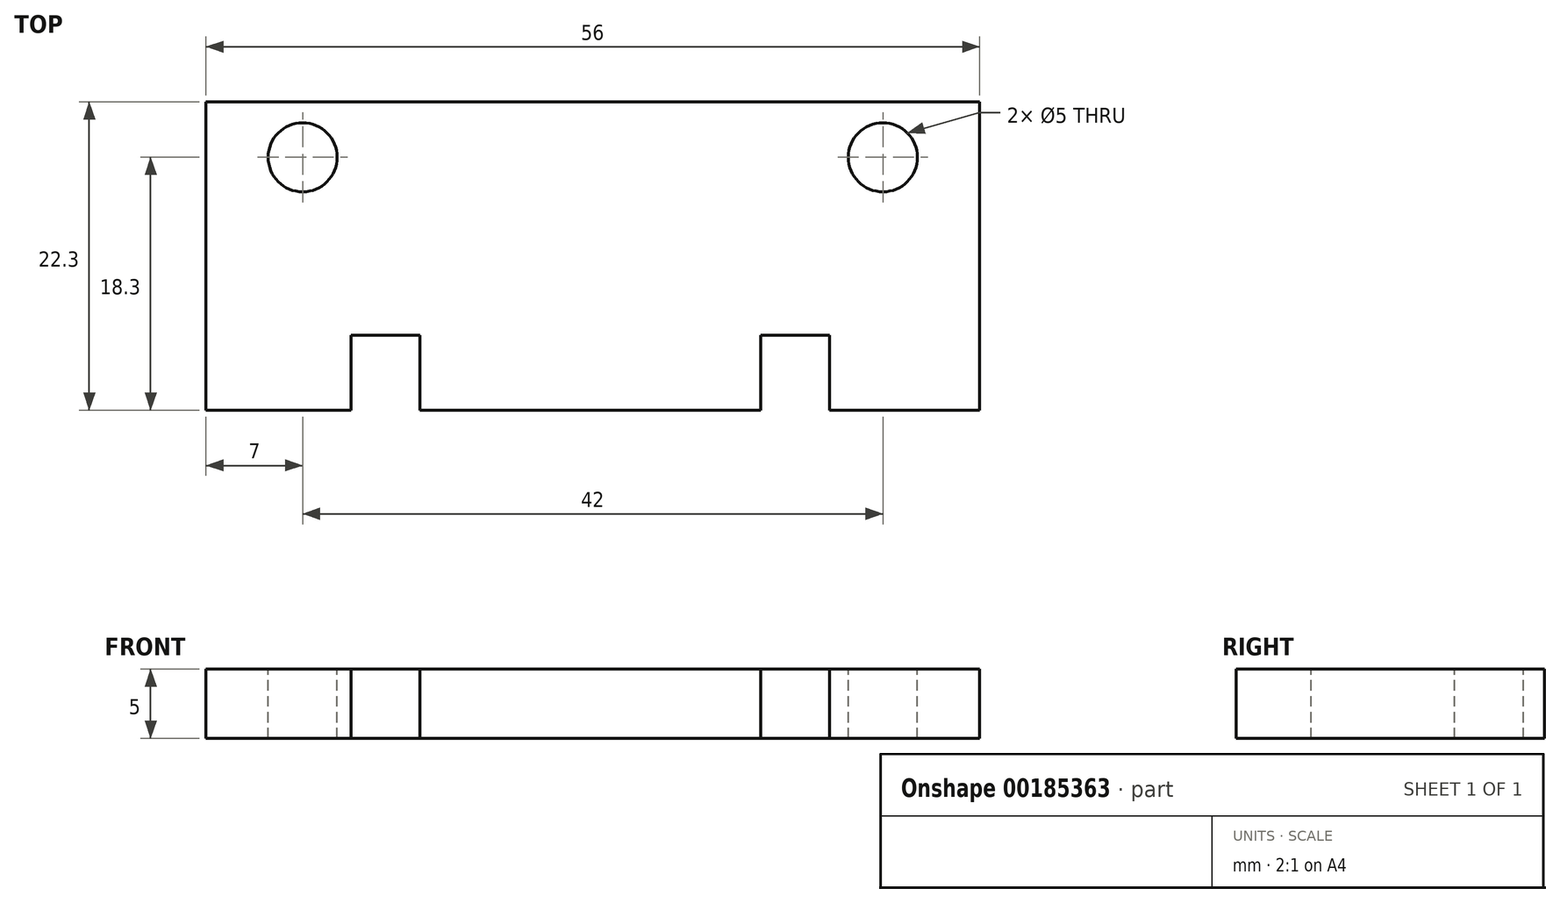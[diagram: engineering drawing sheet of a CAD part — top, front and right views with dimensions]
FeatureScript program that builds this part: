
annotation { "Feature Type Name" : "Feature", "Feature Type Description" : "" }
export const myFeature = defineFeature(function(context is Context, id is Id, definition is map)
    precondition{}
    {
        {
            var Q0;
            Q0=qCreatedBy(makeId("Top.planeOp"),FACE);
            var sketch = newSketch(context, id + "F0", { "sketchPlane" : qUnion([Q0])});
            skLineSegment(sketch, "E0.bottom", {"start": v(28, -8.65) * mm, "end": v(-28, -8.65) * mm, "construction": true});
            skLineSegment(sketch, "E0.top", {"start": v(28, 8.65) * mm, "end": v(-28, 8.65) * mm});
            skLineSegment(sketch, "E0.left", {"start": v(28, -8.65) * mm, "end": v(28, 8.65) * mm});
            skLineSegment(sketch, "E0.right", {"start": v(-28, -8.65) * mm, "end": v(-28, 8.65) * mm});
            skPoint(sketch, "E0.middle", {"position": v(0, 0) * mm});
            skLineSegment(sketch, "E1", {"start": v(-28, -8.65) * mm, "end": v(-28, -13.65) * mm});
            skLineSegment(sketch, "E2", {"start": v(-28, -13.65) * mm, "end": v(28, -13.65) * mm});
            skLineSegment(sketch, "E3", {"start": v(28, -13.65) * mm, "end": v(28, -8.65) * mm});
            skSolve(sketch);
        }
        {
            var Q0;
            Q0=makeQuery(id+"F0.imprint","IMPRINT",FACE,{"disambiguationData":[TD([[makeQuery(id+"F0.imprint","IMPRINT",EDGE,{"derivedFrom":sQuery(id+"F0.wireOp",EDGE,"E0.top")}),1.0]])]});
            extrude(context, id + "F1", {"entities" : qUnion([Q0]), "depth" : 5 * mm});
        }
        {
            var Q0;
            Q0=makeQuery(id+"F1.opExtrude","CAP_FACE",FACE,{"disambiguationData":[OSD([sQuery(id+"F0.wireOp",EDGE,"E0.bottom"),sQuery(id+"F0.wireOp",EDGE,"E0.top"),sQuery(id+"F0.wireOp",EDGE,"E0.left"),sQuery(id+"F0.wireOp",EDGE,"E0.right")])],"isStart":false});
            var sketch = newSketch(context, id + "F2", { "sketchPlane" : qUnion([Q0])});
            skCircle(sketch, "E4", {"center": v(-21, 4.65) * mm, "radius": 2.5 * mm});
            skCircle(sketch, "E5", {"center": v(21, 4.65) * mm, "radius": 2.5 * mm});
            skLineSegment(sketch, "E6", {"start": v(-28, 4.65) * mm, "end": v(28, 4.65) * mm, "construction": true});
            skLineSegment(sketch, "E7", {"start": v(-21, 4.65) * mm, "end": v(0, 0) * mm});
            skLineSegment(sketch, "E8", {"start": v(0, 0) * mm, "end": v(21, 4.65) * mm});
            skSolve(sketch);
        }
        {
            var Q0;
            Q0 = qSketchRegion(id + "F2", true);
            extrude(context, id + "F3", {"entities" : qUnion([Q0]), "operationType" : NewBodyOperationType.REMOVE, "oppositeDirection" : true, "depth" : 5 * mm});
        }
        {
            var Q0;
            Q0=makeQuery(id+"F1.opExtrude","CAP_FACE",FACE,{"disambiguationData":[OSD([sQuery(id+"F0.wireOp",EDGE,"E0.top"),sQuery(id+"F0.wireOp",EDGE,"E0.left"),sQuery(id+"F0.wireOp",EDGE,"E0.right"),sQuery(id+"F0.wireOp",EDGE,"E1"),sQuery(id+"F0.wireOp",EDGE,"E2"),sQuery(id+"F0.wireOp",EDGE,"E3")])],"isStart":false});
            var sketch = newSketch(context, id + "F4", { "sketchPlane" : qUnion([Q0])});
            skLineSegment(sketch, "E9.bottom", {"start": v(-17.5, -13.65) * mm, "end": v(-12.5, -13.65) * mm});
            skLineSegment(sketch, "E9.top", {"start": v(-17.5, -8.23) * mm, "end": v(-12.5, -8.23) * mm});
            skLineSegment(sketch, "E9.left", {"start": v(-17.5, -13.65) * mm, "end": v(-17.5, -8.23) * mm});
            skLineSegment(sketch, "E9.right", {"start": v(-12.5, -13.65) * mm, "end": v(-12.5, -8.23) * mm});
            skLineSegment(sketch, "E10.bottom", {"start": v(12.14, -13.65) * mm, "end": v(17.14, -13.65) * mm});
            skLineSegment(sketch, "E10.top", {"start": v(12.14, -8.23) * mm, "end": v(17.14, -8.23) * mm});
            skLineSegment(sketch, "E10.left", {"start": v(12.14, -13.65) * mm, "end": v(12.14, -8.23) * mm});
            skLineSegment(sketch, "E10.right", {"start": v(17.14, -13.65) * mm, "end": v(17.14, -8.23) * mm});
            skLineSegment(sketch, "E11", {"start": v(-12.5, -8.23) * mm, "end": v(0, -8.23) * mm, "construction": true});
            skLineSegment(sketch, "E12", {"start": v(0, -8.23) * mm, "end": v(12.5, -8.23) * mm, "construction": true});
            skSolve(sketch);
        }
        {
            var Q0;
            Q0 = qSketchRegion(id + "F4", true);
            extrude(context, id + "F5", {"entities" : qUnion([Q0]), "operationType" : NewBodyOperationType.REMOVE, "oppositeDirection" : true, "depth" : 5 * mm});
        }
    });
